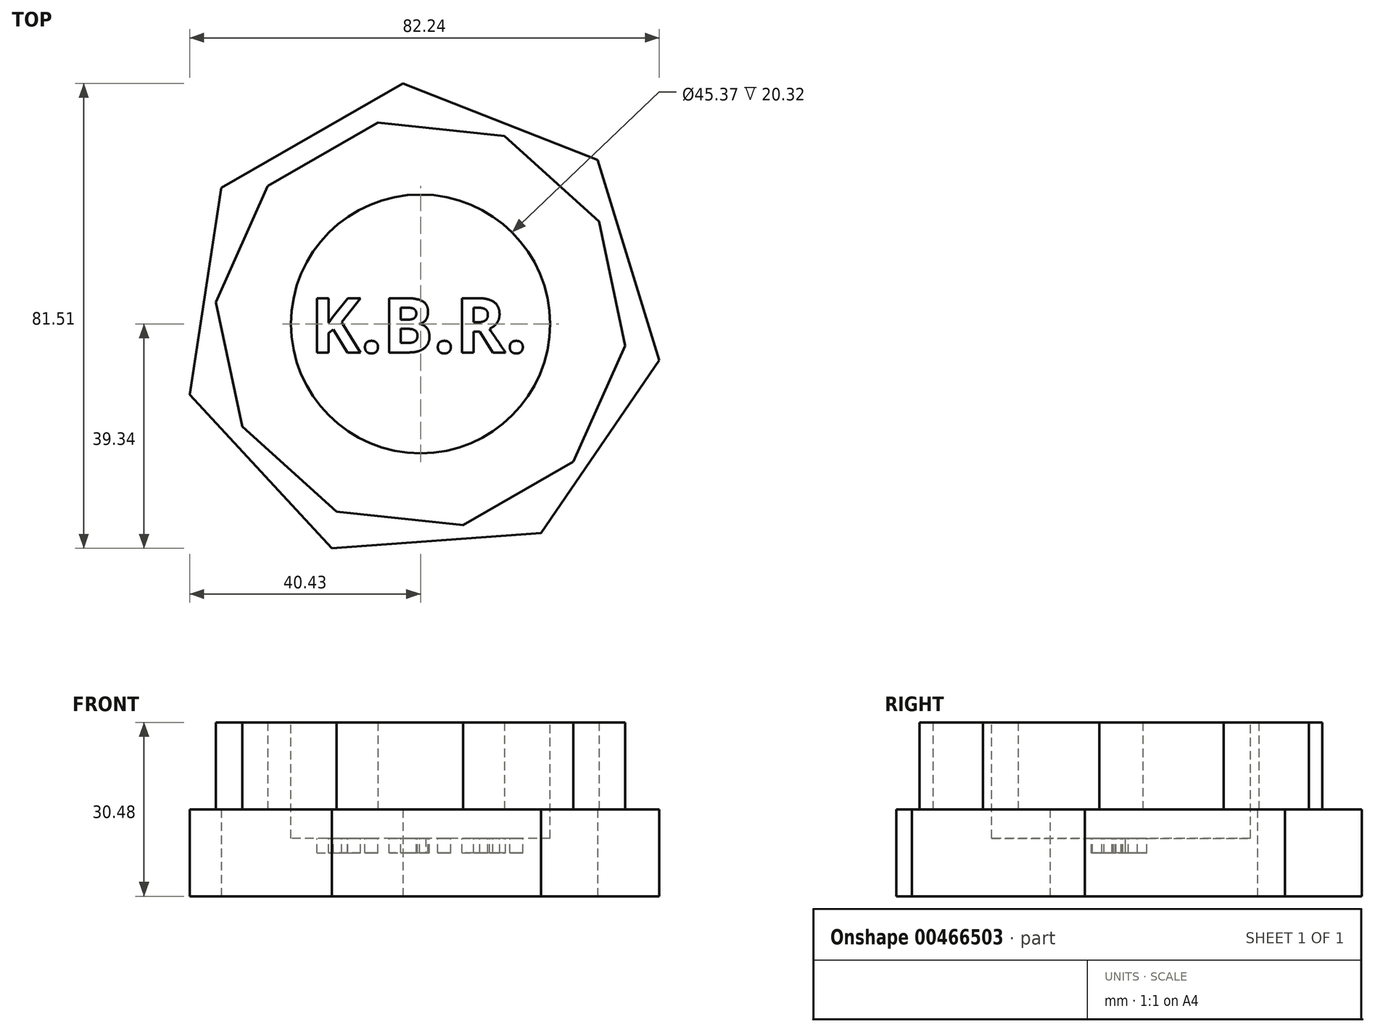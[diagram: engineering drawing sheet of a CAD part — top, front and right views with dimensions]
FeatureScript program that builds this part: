
annotation { "Feature Type Name" : "Feature", "Feature Type Description" : "" }
export const myFeature = defineFeature(function(context is Context, id is Id, definition is map)
    precondition{}
    {
        {
            var Q0;
            Q0=qCreatedBy(makeId("Top.planeOp"),FACE);
            var sketch = newSketch(context, id + "F0", { "sketchPlane" : qUnion([Q0])});
            skCircle(sketch, "E0.cCircle", {"center": v(0, 0) * mm, "radius": 38.1 * mm, "construction": true});
            skLineSegment(sketch, "E0.0", {"start": v(-34.9, 23.87) * mm, "end": v(-3.1, 42.17) * mm});
            skLineSegment(sketch, "E0.1", {"start": v(-3.1, 42.17) * mm, "end": v(31.04, 28.72) * mm});
            skLineSegment(sketch, "E0.2", {"start": v(31.04, 28.72) * mm, "end": v(41.8, -6.36) * mm});
            skLineSegment(sketch, "E0.3", {"start": v(41.8, -6.36) * mm, "end": v(21.1, -36.65) * mm});
            skLineSegment(sketch, "E0.4", {"start": v(21.1, -36.65) * mm, "end": v(-15.5, -39.34) * mm});
            skLineSegment(sketch, "E0.5", {"start": v(-15.5, -39.34) * mm, "end": v(-40.43, -12.41) * mm});
            skLineSegment(sketch, "E0.6", {"start": v(-40.43, -12.41) * mm, "end": v(-34.9, 23.87) * mm});
            skPoint(sketch, "E0.0.midPoint", {"position": v(-19, 33.02) * mm});
            skSolve(sketch);
        }
        {
            var Q0;
            Q0 = qSketchRegion(id + "F0", true);
            extrude(context, id + "F1", {"entities" : qUnion([Q0]), "depth" : 15.24 * mm});
        }
        {
            var Q0;
            Q0=makeQuery(id+"F1.opExtrude","CAP_FACE",FACE,{"disambiguationData":[OSD([sQuery(id+"F0.wireOp",EDGE,"E0.0"),sQuery(id+"F0.wireOp",EDGE,"E0.1"),sQuery(id+"F0.wireOp",EDGE,"E0.2"),sQuery(id+"F0.wireOp",EDGE,"E0.3"),sQuery(id+"F0.wireOp",EDGE,"E0.4"),sQuery(id+"F0.wireOp",EDGE,"E0.5"),sQuery(id+"F0.wireOp",EDGE,"E0.6")])],"isStart":false});
            var sketch = newSketch(context, id + "F2", { "sketchPlane" : qUnion([Q0])});
            skCircle(sketch, "E1.cCircle", {"center": v(0, 0) * mm, "radius": 34.3 * mm, "construction": true});
            skLineSegment(sketch, "E1.0", {"start": v(-26.76, 24.16) * mm, "end": v(-7.45, 35.28) * mm});
            skLineSegment(sketch, "E1.1", {"start": v(-7.45, 35.28) * mm, "end": v(14.7, 32.92) * mm});
            skLineSegment(sketch, "E1.2", {"start": v(14.7, 32.92) * mm, "end": v(31.25, 17.99) * mm});
            skLineSegment(sketch, "E1.3", {"start": v(31.25, 17.99) * mm, "end": v(35.85, -3.82) * mm});
            skLineSegment(sketch, "E1.4", {"start": v(35.85, -3.82) * mm, "end": v(26.76, -24.16) * mm});
            skLineSegment(sketch, "E1.5", {"start": v(26.76, -24.16) * mm, "end": v(7.45, -35.28) * mm});
            skLineSegment(sketch, "E1.6", {"start": v(7.45, -35.28) * mm, "end": v(-14.7, -32.92) * mm});
            skLineSegment(sketch, "E1.7", {"start": v(-14.7, -32.92) * mm, "end": v(-31.25, -17.99) * mm});
            skLineSegment(sketch, "E1.8", {"start": v(-31.25, -17.99) * mm, "end": v(-35.85, 3.82) * mm});
            skLineSegment(sketch, "E1.9", {"start": v(-35.85, 3.82) * mm, "end": v(-26.76, 24.16) * mm});
            skPoint(sketch, "E1.0.midPoint", {"position": v(-17.1, 29.72) * mm});
            skSolve(sketch);
        }
        {
            var Q0;
            Q0 = qSketchRegion(id + "F2", true);
            extrude(context, id + "F3", {"entities" : qUnion([Q0]), "operationType" : NewBodyOperationType.ADD, "depth" : 15.24 * mm});
        }
        {
            var Q0;
            Q0=makeQuery(id+"F3.opExtrude","CAP_FACE",FACE,{"disambiguationData":[OSD([sQuery(id+"F2.wireOp",EDGE,"E1.0"),sQuery(id+"F2.wireOp",EDGE,"E1.1"),sQuery(id+"F2.wireOp",EDGE,"E1.2"),sQuery(id+"F2.wireOp",EDGE,"E1.3"),sQuery(id+"F2.wireOp",EDGE,"E1.4"),sQuery(id+"F2.wireOp",EDGE,"E1.5"),sQuery(id+"F2.wireOp",EDGE,"E1.6"),sQuery(id+"F2.wireOp",EDGE,"E1.7"),sQuery(id+"F2.wireOp",EDGE,"E1.8"),sQuery(id+"F2.wireOp",EDGE,"E1.9")])],"isStart":false});
            var sketch = newSketch(context, id + "F4", { "sketchPlane" : qUnion([Q0])});
            skCircle(sketch, "E2", {"center": v(0, 0) * mm, "radius": 22.68 * mm});
            skSolve(sketch);
        }
        {
            var Q0;
            Q0=makeQuery(id+"F4.imprint","IMPRINT",FACE,{"disambiguationData":[TD([[makeQuery(id+"F4.imprint","IMPRINT",EDGE,{"derivedFrom":sQuery(id+"F4.wireOp",EDGE,"E2")}),1.0]])]});
            var Q1;
            Q1=sQuery(id+"F4.wireOp",EDGE,"E2");
            extrude(context, id + "F5", {"entities" : qUnion([Q0]), "operationType" : NewBodyOperationType.REMOVE, "surfaceEntities" : qUnion([Q1]), "oppositeDirection" : true, "depth" : 20.32 * mm});
        }
        {
            var Q0;
            Q0=makeQuery(id+"F5.boolean.opBoolean","COPY",FACE,{"derivedFrom":makeQuery(id+"F5.opExtrude","CAP_FACE",FACE,{"disambiguationData":[OSD([sQuery(id+"F4.wireOp",EDGE,"E2")])],"isStart":false})});
            var sketch = newSketch(context, id + "F6", { "sketchPlane" : qUnion([Q0])});
            skText(sketch, "E3", { "text": "K.B.R.", "fontName": "OpenSans-Bold.ttf"});
            const initialGuessF6  = {"E3": [-0.01935, -0.005, 1, 0, 0.0096]};
            skSetInitialGuess(sketch, initialGuessF6);
            skSolve(sketch);
        }
        {
            var Q0;
            Q0 = qSketchRegion(id + "F6", true);
            extrude(context, id + "F7", {"entities" : qUnion([Q0]), "operationType" : NewBodyOperationType.REMOVE, "oppositeDirection" : true, "depth" : 2.54 * mm});
        }
    });
